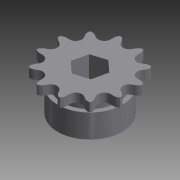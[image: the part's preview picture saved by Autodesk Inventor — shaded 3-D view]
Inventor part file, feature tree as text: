
AUTODESK INVENTOR PART (.ipt)
format: ipt  version: 2013 (Build 170138000, 138)  size: 260,096 bytes
history: native  units: mm (DEFAULTED — no unit token found)
features: extrude x2, sketch x2, imported_body x1
ambient origin geometry x8: Origin, YZ Plane, XZ Plane, XY Plane, X Axis, Y Axis, Z Axis, Center Point
bodies: Solid1 (feature_tree)
feature tree (5):
  imported_body  "Base1"
  extrude  "Extrusion1"  Depth=12.7mm
  extrude  "Extrusion2"  [1 undecoded]
  sketch  "Sketch1"  dims[d0=19.2532mm d1=0.0mm d2=12.7mm]
  sketch  "Sketch2"  dims[d3=19.2532mm d4=0.0mm]
note: 1 required parameter value undecoded (feature->parameter linkage not recoverable at this tier; creation-order binding heuristic only, values carry confidence <= 0.55)
